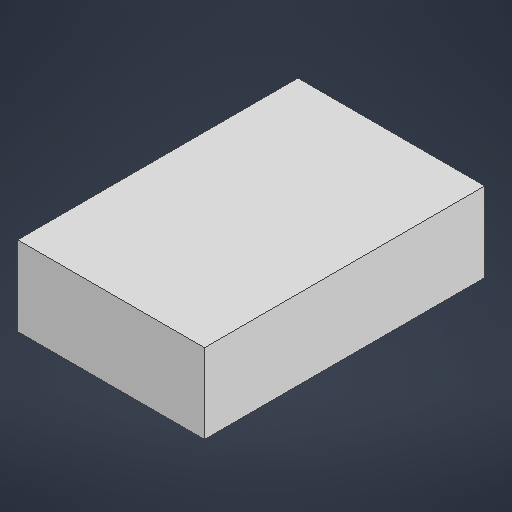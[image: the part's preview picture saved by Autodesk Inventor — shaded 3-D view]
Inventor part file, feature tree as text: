
AUTODESK INVENTOR PART (.ipt)
format: ipt  version: 2025.2 (Build 292293000, 293)  size: 161,792 bytes
history: native  units: mm
features: extrude x2, sketch x2
ambient origin geometry x8: Origin, YZ Plane, XZ Plane, XY Plane, X Axis, Y Axis, Z Axis, Center Point
bodies: Solid1 (feature_tree)
feature tree (4):
  extrude  "Extrusion1"  Depth=88.19mm
  extrude  "Extrusion2"  Depth=11.0mm
  sketch  "Sketch2"  dims[d0=58.8mm d1=88.19mm]
  sketch  "Sketch3"  dims[d2=25.0mm d3=0.0mm d4=11.0mm d5=1.0mm d6=7.0mm d7=3.0mm d8=0.0mm]
